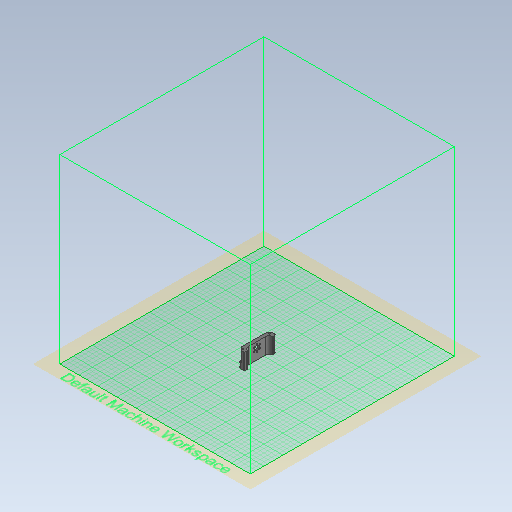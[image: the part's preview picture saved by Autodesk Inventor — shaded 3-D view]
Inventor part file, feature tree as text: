
AUTODESK INVENTOR PART (.ipt)
format: ipt  version: 2020 (Build 240168000, 168)  size: 628,224 bytes
history: native  units: mm
features: sketch x9, extrude x8, chamfer x3, projected_geometry x3, other x1, fillet x1
ambient origin geometry x8: Origin, YZ Plane, XZ Plane, XY Plane, X Axis, Y Axis, Z Axis, Center Point
bodies: Body1 (feature_tree)
feature tree (25):
  other  "Твердое тело1"
  extrude  "Выдавливание1"  Depth=35.0mm TaperAngle=0.0deg
  sketch  "Эскиз2"
  extrude  "Выдавливание4"  Depth=20.6mm
  extrude  "Выдавливание5"  Depth=15.0mm
  sketch  "Эскиз5"
  extrude  "Выдавливание8"  Depth=2.5mm
  extrude  "Выдавливание9"  Depth=60.0mm TaperAngle=360.0deg
  chamfer  "Фаска2"  Distance=11.0mm
  sketch  "Эскиз6"
  extrude  "Выдавливание10"  Depth=3.8mm
  fillet  "Сопряжение1"  Radius=3.8mm
  extrude  "Выдавливание11"  Depth=40.5mm TaperAngle=0.0deg
  extrude  "Выдавливание12"  Depth=4.0mm
  chamfer  "Фаска3"  Distance=4.0mm
  chamfer  "Фаска4"  Distance=3.5mm
  sketch  "Эскиз1"
  projected_geometry  "Спроецированная петля1"
  sketch  "Эскиз3"
  sketch  "Эскиз4"
  projected_geometry  "Спроецированная петля2"
  sketch  "Эскиз7"
  sketch  "Эскиз8"
  projected_geometry  "Спроецированная петля3"
  sketch  "Эскиз9"
